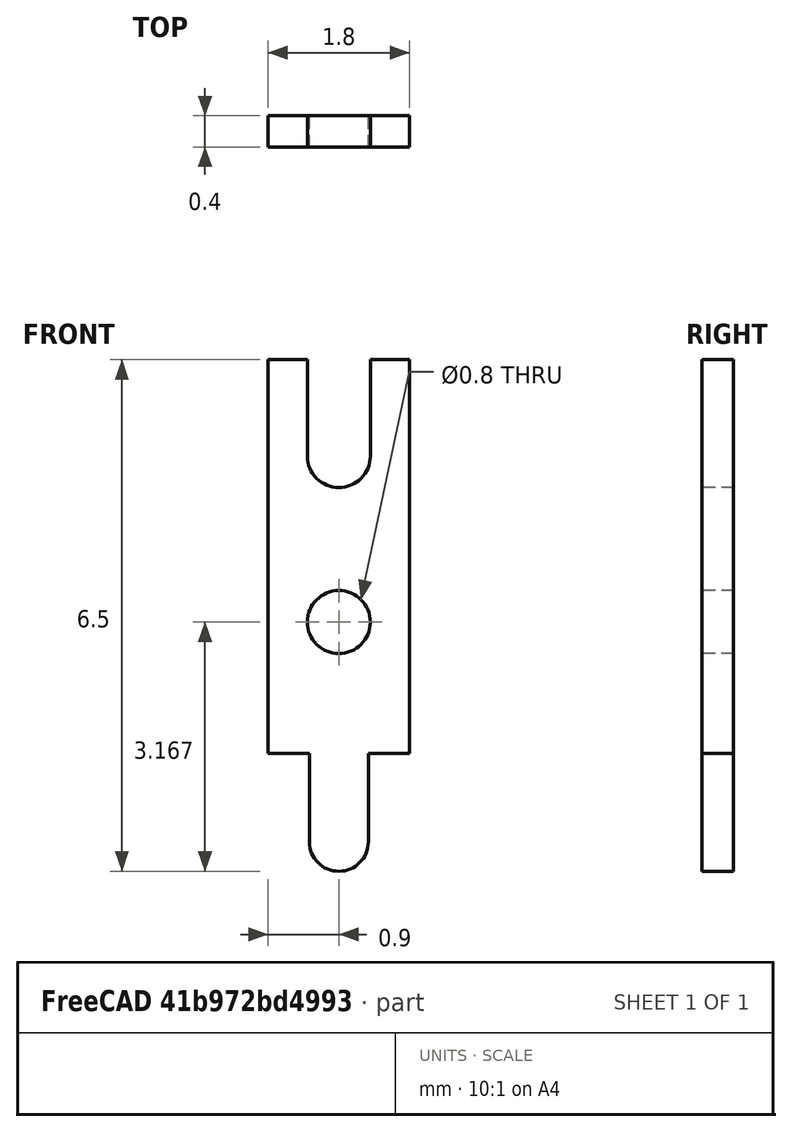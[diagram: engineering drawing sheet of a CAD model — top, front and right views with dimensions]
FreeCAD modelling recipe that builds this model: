
FCSTD DOCUMENT  (FreeCAD 0.17R12018 (Git))
Label: Pin_d0.7mm_L6.5mm_W1.8mm_FlatFork
License: All rights reserved
LicenseURL: http://en.wikipedia.org/wiki/All_rights_reserved
objects: Spreadsheet::Sheet×1, Sketcher::SketchObject×1, PartDesign::Pad×1, PartDesign::Body×1, App::Part×1
note: 4 computed .brp shape members not serialized (recipe doc carries the construction recipe); baked Part::Feature solids carry a one-line shape summary decoded from their .brp

FEATURE [Spreadsheet::Sheet] Spreadsheet  label="dimensions"
  cells = A1="L"; B1(L)=6.5; A2="Wtop"; B2(Wtop)=1.8; A3="Wbottom"; B3(Wbottom)=0.75; A4="Lbottom"; B4(Lbottom)=1.5; A5="Wfork"; B5(Wfork)=0.80000000000000004; A6="FractionFork"; B6(FractionFork)=0.25; A7="thick"; B7(thick)=0.40000000000000002
FEATURE [Sketcher::SketchObject] Sketch
  MapMode = 5
  Placement = pos=(0,0,0) rot=(0,0.707107,0.707107;3.14159rad)
  Support = -> [XZ_Plane001]
  expr: Constraints[44] = (dimensions.L - dimensions.Lbottom) * 0.66669999999999996
  expr: Constraints[43] = dimensions.Wfork / 2
  expr: Constraints[40] = dimensions.Wtop
  expr: Constraints[38] = dimensions.Wbottom
  expr: Constraints[39] = (dimensions.Wtop - dimensions.Wbottom) / 2
  expr: Constraints[37] = dimensions.Lbottom - dimensions.Wbottom / 2
  expr: Constraints[32] = dimensions.L - dimensions.Lbottom
  expr: Constraints[19] = dimensions.Wfork
  sketch-geometry (15):
    g0: LineSegment StartX=-0.9 StartY=5 StartZ=0 EndX=-0.9 EndY=0 EndZ=0
    g1: LineSegment StartX=-0.9 StartY=0 StartZ=0 EndX=-0.375 EndY=0 EndZ=0
    g2: LineSegment StartX=-0.375 StartY=0 StartZ=0 EndX=-0.375 EndY=-1.125 EndZ=0
    g3: LineSegment StartX=0.375 StartY=0 StartZ=0 EndX=0.375 EndY=-1.125 EndZ=0
    g4: LineSegment StartX=0.375 StartY=0 StartZ=0 EndX=0.9 EndY=0 EndZ=0
    g5: LineSegment StartX=0.9 StartY=0 StartZ=0 EndX=0.9 EndY=5 EndZ=0
    g6: LineSegment StartX=0.9 StartY=5 StartZ=0 EndX=0.4 EndY=5 EndZ=0
    g7: LineSegment StartX=0.4 StartY=5 StartZ=0 EndX=0.4 EndY=3.775 EndZ=0
    g8: LineSegment StartX=-0.4 StartY=3.775 StartZ=0 EndX=-0.4 EndY=5 EndZ=0
    g9: LineSegment StartX=-0.4 StartY=5 StartZ=0 EndX=-0.9 EndY=5 EndZ=0
    g10: ArcOfCircle CenterX=0 CenterY=-1.125 CenterZ=0 NormalX=0 NormalY=0 NormalZ=1 Radius=0.375 StartAngle=3.14159 EndAngle=6.28319
    g11: ArcOfCircle CenterX=0 CenterY=3.775 CenterZ=0 NormalX=0 NormalY=0 NormalZ=1 Radius=0.4 StartAngle=3.14159 EndAngle=6.28319
    g12: LineSegment [constr] StartX=-0.375 StartY=-1.125 StartZ=0 EndX=0.375 EndY=-1.125 EndZ=0
    g13: LineSegment [constr] StartX=-0.4 StartY=3.775 StartZ=0 EndX=0.4 EndY=3.775 EndZ=0
    g14: Circle CenterX=0 CenterY=1.6665 CenterZ=0 NormalX=0 NormalY=0 NormalZ=1 Radius=0.4
  constraints (45):
    c: PointOnObject(g3,g-1)
    c: Horizontal(g6)
    c: Vertical(g7)
    c: Vertical(g8)
    c: Coincident(g9,g0)
    c: Horizontal(g9)
    c: Equal(g9,g6)
    c: PointOnObject(g10,g-2)
    c: Coincident(g8,g9)
    c: Coincident(g6,g7)
    c: Coincident(g5,g6)
    c: Coincident(g11,g8)
    c: Coincident(g11,g7)
    c: Coincident(g12,g3)
    c: Coincident(g13,g8)
    c: Coincident(g13,g7)
    c: Horizontal(g13)
    c: PointOnObject(g11,g13)
    c: DistanceY(g8,g6) = 0
    c: DistanceX(g8,g6) = 0.8
    c: DistanceY(g8,g8) = 1.225
    c: Coincident(g12,g2)
    c: Coincident(g2,g10)
    c: Coincident(g3,g10)
    c: PointOnObject(g10,g12)
    c: Horizontal(g12)
    c: Vertical(g3)
    c: Vertical(g2)
    c: Horizontal(g1)
    c: Horizontal(g4)
    c: Vertical(g5)
    c: Vertical(g0)
    c: DistanceY(g5,g5) = 5
    c: Coincident(g5,g4)
    c: Coincident(g0,g1)
    c: Coincident(g4,g3)
    c: Coincident(g1,g2)
    c: DistanceY(g3,g3) = 1.125
    c: DistanceX(g2,g3) = 0.75
    c: DistanceX(g1,g1) = 0.525
    c: DistanceX(g0,g5) = 1.8
    c: PointOnObject(g1,g-1)
    c: PointOnObject(g14,g-2)
    c: Radius(g14) = 0.4
    c: DistanceY(g14,g8) = 3.3335
FEATURE [PartDesign::Pad] Pad
  Length = 0.4
  Length2 = 100
  Midplane = true
  Placement = pos=(0,0,0) rot=(1,0,0;1.5708rad)
  Profile = -> Sketch
  Type = 0
  expr: Length = dimensions.thick
FEATURE [PartDesign::Body] PadBody  label="Pin_d0.7mm_L6.5mm_W1.8mm_FlatFork "
  Group = -> [Sketch,Pad]
  Origin = -> Origin001
  Tip = -> Pad
FEATURE [App::Part] Part  label="Body1"
  Group = -> [PadBody]
  License = CC BY 3.0
  LicenseURL = http://creativecommons.org/licenses/by/3.0/
  Origin = -> Origin
